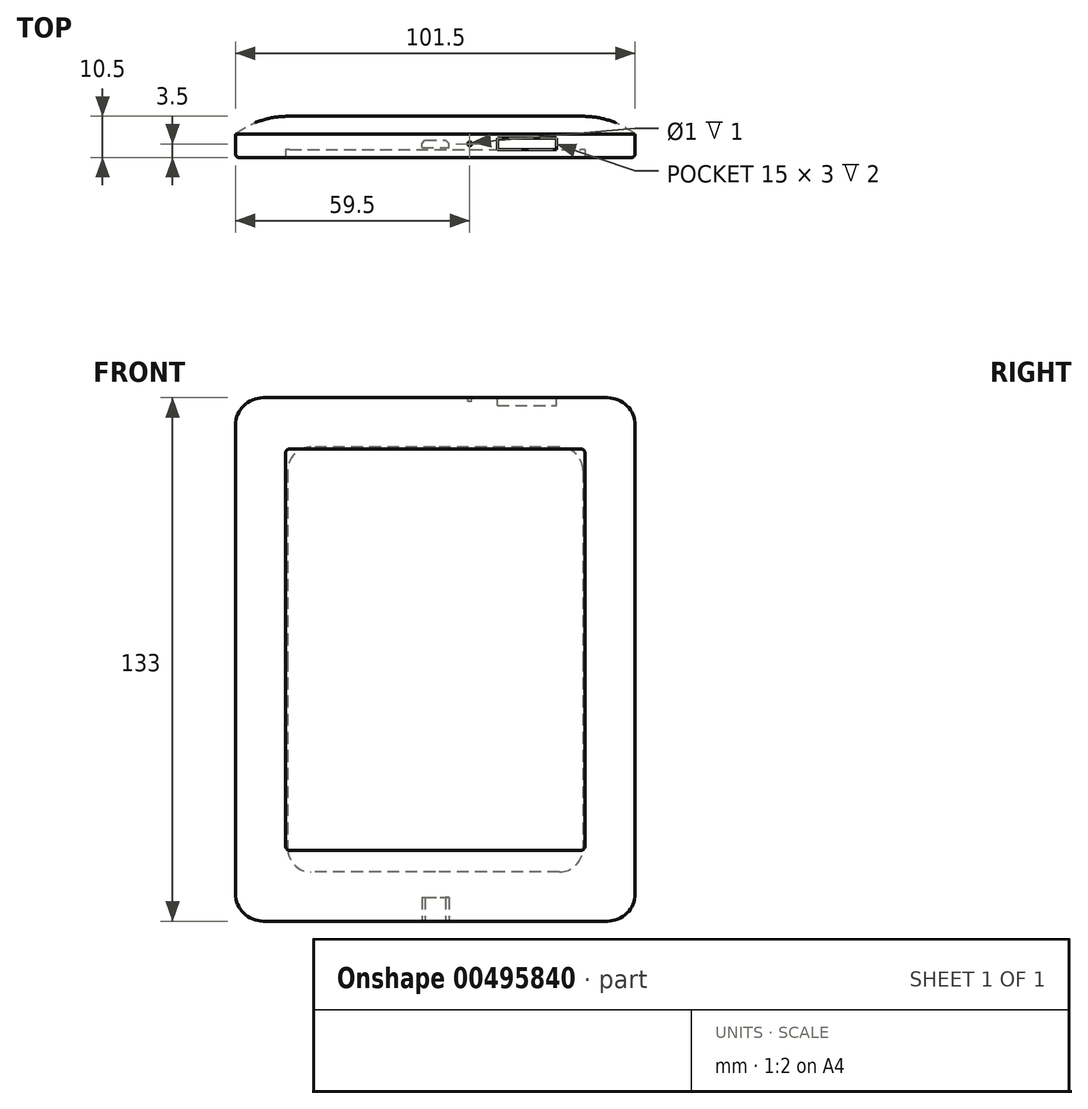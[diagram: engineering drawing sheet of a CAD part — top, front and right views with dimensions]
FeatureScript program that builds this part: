
annotation { "Feature Type Name" : "Feature", "Feature Type Description" : "" }
export const myFeature = defineFeature(function(context is Context, id is Id, definition is map)
    precondition{}
    {
        {
            var Q0;
            Q0=qCreatedBy(makeId("Front.planeOp"),FACE);
            var sketch = newSketch(context, id + "F0", { "sketchPlane" : qUnion([Q0])});
            skLineSegment(sketch, "E0.bottom", {"start": v(-43.75, 66.5) * mm, "end": v(43.75, 66.5) * mm});
            skLineSegment(sketch, "E0.top", {"start": v(-43.75, -66.5) * mm, "end": v(43.75, -66.5) * mm});
            skLineSegment(sketch, "E0.left", {"start": v(-50.75, 59.5) * mm, "end": v(-50.75, -59.5) * mm});
            skLineSegment(sketch, "E0.right", {"start": v(50.75, 59.5) * mm, "end": v(50.75, -59.5) * mm});
            skPoint(sketch, "E1.visualSharp", {"position": v(-50.75, 66.5) * mm});
            skArc(sketch, "E1.filletArc", {"start": v(-43.75, 66.5) * mm, "mid": v(-48.7, 64.45) * mm, "end": v(-50.75, 59.5) * mm});
            skPoint(sketch, "E2.visualSharp", {"position": v(50.75, 66.5) * mm});
            skArc(sketch, "E2.filletArc", {"start": v(50.75, 59.5) * mm, "mid": v(48.7, 64.45) * mm, "end": v(43.75, 66.5) * mm});
            skPoint(sketch, "E3.visualSharp", {"position": v(53.07, -60.42) * mm});
            skArc(sketch, "E3.filletArc", {"start": v(43.75, -66.5) * mm, "mid": v(48.7, -64.45) * mm, "end": v(50.75, -59.5) * mm});
            skPoint(sketch, "E4.visualSharp", {"position": v(-50.75, -66.5) * mm});
            skArc(sketch, "E4.filletArc", {"start": v(-50.75, -59.5) * mm, "mid": v(-48.7, -64.45) * mm, "end": v(-43.75, -66.5) * mm});
            skLineSegment(sketch, "E5", {"start": v(50.75, 66.5) * mm, "end": v(-50.75, -66.5) * mm, "construction": true});
            skSolve(sketch);
        }
        {
            var Q0;
            Q0 = qSketchRegion(id + "F0", true);
            extrude(context, id + "F1", {"entities" : qUnion([Q0]), "depth" : 10.5 * mm});
        }
        {
            var Q0;
            Q0=makeQuery(id+"F1.opExtrude","CAP_FACE",FACE,{"disambiguationData":[OSD([sQuery(id+"F0.wireOp",EDGE,"E0.bottom"),sQuery(id+"F0.wireOp",EDGE,"E0.top"),sQuery(id+"F0.wireOp",EDGE,"E0.left"),sQuery(id+"F0.wireOp",EDGE,"E0.right"),sQuery(id+"F0.wireOp",EDGE,"E1.filletArc"),sQuery(id+"F0.wireOp",EDGE,"E2.filletArc"),sQuery(id+"F0.wireOp",EDGE,"E3.filletArc"),sQuery(id+"F0.wireOp",EDGE,"E4.filletArc")])],"isStart":false});
            var sketch = newSketch(context, id + "F2", { "sketchPlane" : qUnion([Q0])});
            skLineSegment(sketch, "E6.bottom", {"start": v(-37, 53.5) * mm, "end": v(37, 53.5) * mm});
            skLineSegment(sketch, "E6.top", {"start": v(-37, -48.5) * mm, "end": v(37, -48.5) * mm});
            skLineSegment(sketch, "E6.left", {"start": v(-38, 52.5) * mm, "end": v(-38, -47.5) * mm});
            skLineSegment(sketch, "E6.right", {"start": v(38, 52.5) * mm, "end": v(38, -47.5) * mm});
            skLineSegment(sketch, "E7", {"start": v(0, 205.93) * mm, "end": v(0, -99.52) * mm, "construction": true});
            skLineSegment(sketch, "E8", {"start": v(-176.83, 0) * mm, "end": v(104.16, 0) * mm, "construction": true});
            skPoint(sketch, "E9.visualSharp", {"position": v(-38, 53.5) * mm});
            skArc(sketch, "E9.filletArc", {"start": v(-37, 53.5) * mm, "mid": v(-37.7, 53.2) * mm, "end": v(-38, 52.5) * mm});
            skPoint(sketch, "E10.visualSharp", {"position": v(38, 53.5) * mm});
            skArc(sketch, "E10.filletArc", {"start": v(38, 52.5) * mm, "mid": v(37.7, 53.2) * mm, "end": v(37, 53.5) * mm});
            skPoint(sketch, "E11.visualSharp", {"position": v(38, -48.5) * mm});
            skArc(sketch, "E11.filletArc", {"start": v(37, -48.5) * mm, "mid": v(37.7, -48.2) * mm, "end": v(38, -47.5) * mm});
            skPoint(sketch, "E12.visualSharp", {"position": v(-38, -48.5) * mm});
            skArc(sketch, "E12.filletArc", {"start": v(-38, -47.5) * mm, "mid": v(-37.7, -48.2) * mm, "end": v(-37, -48.5) * mm});
            skSolve(sketch);
        }
        {
            var Q0;
            Q0 = qSketchRegion(id + "F2", true);
            extrude(context, id + "F3", {"entities" : qUnion([Q0]), "operationType" : NewBodyOperationType.REMOVE, "oppositeDirection" : true, "depth" : 2 * mm});
        }
        {
            var Q0;
            Q0=makeQuery(id+"F1.opExtrude","CAP_EDGE",EDGE,{"disambiguationData":[OSD([sQuery(id+"F0.wireOp",EDGE,"E0.bottom")])],"isStart":false});
            fillet(context, id + "F4", {"entities" : qUnion([Q0]), "radius" : 1 * mm, "tangentPropagation" : true, "allowEdgeOverflow" : false});
        }
        {
            var Q0;
            Q0=qCreatedBy(makeId("Top.planeOp"),FACE);
            var sketch = newSketch(context, id + "F5", { "sketchPlane" : qUnion([Q0])});
            skArc(sketch, "E13", {"start": v(50.75, -4.5) * mm, "mid": v(44.5, -1.16) * mm, "end": v(37.5, 0) * mm});
            skLineSegment(sketch, "E14", {"start": v(37.5, 0) * mm, "end": v(50.75, 0) * mm});
            skLineSegment(sketch, "E15", {"start": v(50.75, 0) * mm, "end": v(50.75, -4.5) * mm});
            skLineSegment(sketch, "E16", {"start": v(-50.75, 0) * mm, "end": v(-37.5, 0) * mm, "construction": true});
            skSolve(sketch);
        }
        {
            var Q0;
            Q0=makeQuery(id+"F1.opExtrude","CAP_FACE",FACE,{"disambiguationData":[OSD([sQuery(id+"F0.wireOp",EDGE,"E0.bottom"),sQuery(id+"F0.wireOp",EDGE,"E0.top"),sQuery(id+"F0.wireOp",EDGE,"E0.left"),sQuery(id+"F0.wireOp",EDGE,"E0.right"),sQuery(id+"F0.wireOp",EDGE,"E1.filletArc"),sQuery(id+"F0.wireOp",EDGE,"E2.filletArc"),sQuery(id+"F0.wireOp",EDGE,"E3.filletArc"),sQuery(id+"F0.wireOp",EDGE,"E4.filletArc")])],"isStart":true});
            var sketch = newSketch(context, id + "F6", { "sketchPlane" : qUnion([Q0])});
            skLineSegment(sketch, "E17.bottom", {"start": v(-31.5, 54) * mm, "end": v(31.5, 54) * mm});
            skLineSegment(sketch, "E17.top", {"start": v(-31.5, -54) * mm, "end": v(31.5, -54) * mm});
            skLineSegment(sketch, "E17.left", {"start": v(-37.5, 48) * mm, "end": v(-37.5, -48) * mm});
            skLineSegment(sketch, "E17.right", {"start": v(37.5, 48) * mm, "end": v(37.5, -48) * mm});
            skLineSegment(sketch, "E18", {"start": v(0, 0) * mm, "end": v(154.61, 0) * mm, "construction": true});
            skPoint(sketch, "E19.visualSharp", {"position": v(-37.5, 54) * mm});
            skArc(sketch, "E19.filletArc", {"start": v(-31.5, 54) * mm, "mid": v(-35.74, 52.24) * mm, "end": v(-37.5, 48) * mm});
            skPoint(sketch, "E20.visualSharp", {"position": v(37.5, 54) * mm});
            skArc(sketch, "E20.filletArc", {"start": v(37.5, 48) * mm, "mid": v(35.74, 52.24) * mm, "end": v(31.5, 54) * mm});
            skPoint(sketch, "E21.visualSharp", {"position": v(37.5, -54) * mm});
            skArc(sketch, "E21.filletArc", {"start": v(31.5, -54) * mm, "mid": v(35.74, -52.24) * mm, "end": v(37.5, -48) * mm});
            skPoint(sketch, "E22.visualSharp", {"position": v(-37.5, -54) * mm});
            skArc(sketch, "E22.filletArc", {"start": v(-37.5, -48) * mm, "mid": v(-35.74, -52.24) * mm, "end": v(-31.5, -54) * mm});
            skSolve(sketch);
        }
        {
            var Q0;
            Q0=sQuery(id+"F5.wireOp",VERTEX,"E15.end");
            var Q1;
            Q1=qCreatedBy(makeId("Front.planeOp"),FACE);
            cPlane(context, id + "F7", {"entities" : qUnion([Q0, Q1]), "cplaneType" : CPlaneType.PLANE_POINT, "offset" : 25 * mm, "width" : 150 * mm, "height" : 150 * mm});
        }
        {
            var Q0;
            Q0=qCreatedBy(id+"F7.planeOp",FACE);
            var sketch = newSketch(context, id + "F8", { "sketchPlane" : qUnion([Q0])});
            skArc(sketch, "E23.0.0", {"start": v(-43.75, -66.5) * mm, "mid": v(-48.7, -64.45) * mm, "end": v(-50.75, -59.5) * mm});
            skLineSegment(sketch, "E23.0.1", {"start": v(-50.75, -59.5) * mm, "end": v(-50.75, 59.5) * mm});
            skArc(sketch, "E23.0.2", {"start": v(-50.75, 59.5) * mm, "mid": v(-48.7, 64.45) * mm, "end": v(-43.75, 66.5) * mm});
            skLineSegment(sketch, "E23.0.3", {"start": v(-43.75, 66.5) * mm, "end": v(43.75, 66.5) * mm});
            skArc(sketch, "E23.0.4", {"start": v(43.75, 66.5) * mm, "mid": v(48.7, 64.45) * mm, "end": v(50.75, 59.5) * mm});
            skLineSegment(sketch, "E23.0.5", {"start": v(50.75, 59.5) * mm, "end": v(50.75, -59.5) * mm});
            skArc(sketch, "E23.0.6", {"start": v(50.75, -59.5) * mm, "mid": v(48.7, -64.45) * mm, "end": v(43.75, -66.5) * mm});
            skLineSegment(sketch, "E23.0.7", {"start": v(43.75, -66.5) * mm, "end": v(-43.75, -66.5) * mm});
            skSolve(sketch);
        }
        {
            var Q0;
            Q0=makeQuery(id+"F6.imprint","IMPRINT",FACE,{"disambiguationData":[TD([[makeQuery(id+"F6.imprint","IMPRINT",EDGE,{"derivedFrom":sQuery(id+"F6.wireOp",EDGE,"E17.bottom")}),1.0]])]});
            var sketch = newSketch(context, id + "F9", { "sketchPlane" : qUnion([Q0])});
            skArc(sketch, "E24.0.0", {"start": v(43.75, -66.5) * mm, "mid": v(48.7, -64.45) * mm, "end": v(50.75, -59.5) * mm});
            skLineSegment(sketch, "E24.0.1", {"start": v(50.75, -59.5) * mm, "end": v(50.75, 59.5) * mm});
            skArc(sketch, "E24.0.2", {"start": v(50.75, 59.5) * mm, "mid": v(48.7, 64.45) * mm, "end": v(43.75, 66.5) * mm});
            skLineSegment(sketch, "E24.0.3", {"start": v(43.75, 66.5) * mm, "end": v(-43.75, 66.5) * mm});
            skArc(sketch, "E24.0.4", {"start": v(-43.75, 66.5) * mm, "mid": v(-48.7, 64.45) * mm, "end": v(-50.75, 59.5) * mm});
            skLineSegment(sketch, "E24.0.5", {"start": v(-50.75, 59.5) * mm, "end": v(-50.75, -59.5) * mm});
            skArc(sketch, "E24.0.6", {"start": v(-50.75, -59.5) * mm, "mid": v(-48.7, -64.45) * mm, "end": v(-43.75, -66.5) * mm});
            skLineSegment(sketch, "E24.0.7", {"start": v(-43.75, -66.5) * mm, "end": v(43.75, -66.5) * mm});
            skSolve(sketch);
        }
        {
            var Q1;
            Q1 = qSketchRegion(id + "F5", true);
            var Q2;
            Q2 = qConstructionFilter(qBodyType(qCreatedBy(id + "F6" ,EDGE), BodyType.WIRE), ConstructionObject.NO);
            var Q3;
            Q3 = qConstructionFilter(qBodyType(qCreatedBy(id + "F8" ,EDGE), BodyType.WIRE), ConstructionObject.NO);
            var Q4;
            Q4 = qConstructionFilter(qBodyType(qCreatedBy(id + "F9" ,EDGE), BodyType.WIRE), ConstructionObject.NO);
            loft(context, id + "F10", {"operationType" : NewBodyOperationType.REMOVE, "addGuides" : true, "sheetProfilesArray" : [{ "sheetProfileEntities" : qUnion([Q1]) }], "guidesArray" : [{ "guideEntities" : qUnion([Q2]), "guideDerivativeType" : LoftGuideDerivativeType.DEFAULT, "guideDerivativeMagnitude" : 1 }, { "guideEntities" : qUnion([Q3]), "guideDerivativeType" : LoftGuideDerivativeType.DEFAULT, "guideDerivativeMagnitude" : 1 }, { "guideEntities" : qUnion([Q4]), "guideDerivativeType" : LoftGuideDerivativeType.DEFAULT, "guideDerivativeMagnitude" : 1 }]});
        }
        {
            var Q0;
            Q0=makeQuery(id+"F1.opExtrude","SWEPT_FACE",FACE,{"disambiguationData":[OSD([sQuery(id+"F0.wireOp",EDGE,"E0.top")])]});
            var sketch = newSketch(context, id + "F11", { "sketchPlane" : qUnion([Q0])});
            skLineSegment(sketch, "E25", {"start": v(0, 7) * mm, "end": v(0, -5.98) * mm, "construction": true});
            skLineSegment(sketch, "E26.bottom", {"start": v(-3.43, 7.93) * mm, "end": v(0, 7.93) * mm});
            skLineSegment(sketch, "E26.top", {"start": v(-2.65, 6.08) * mm, "end": v(0, 6.08) * mm});
            skLineSegment(sketch, "E26.left", {"start": v(-3.43, 7.93) * mm, "end": v(-3.43, 6.9) * mm});
            skLineSegment(sketch, "E27", {"start": v(-8.15, 7) * mm, "end": v(7.58, 7) * mm, "construction": true});
            skLineSegment(sketch, "E28", {"start": v(-3.43, 6.9) * mm, "end": v(-2.65, 6.08) * mm});
            skLineSegment(sketch, "E29.MirrorCS", {"start": v(3.42, 7.93) * mm, "end": v(0, 7.93) * mm});
            skLineSegment(sketch, "E30.MirrorCS", {"start": v(3.42, 7.93) * mm, "end": v(3.42, 6.9) * mm});
            skLineSegment(sketch, "E31.MirrorCS", {"start": v(3.42, 6.9) * mm, "end": v(2.65, 6.08) * mm});
            skLineSegment(sketch, "E32.MirrorCS", {"start": v(2.65, 6.08) * mm, "end": v(0, 6.08) * mm});
            skSolve(sketch);
        }
        {
            var Q0;
            Q0 = qSketchRegion(id + "F11", true);
            extrude(context, id + "F12", {"entities" : qUnion([Q0]), "operationType" : NewBodyOperationType.REMOVE, "oppositeDirection" : true, "depth" : 6 * mm});
        }
        {
            var Q0;
            Q0=makeQuery(id+"F1.opExtrude","SWEPT_FACE",FACE,{"disambiguationData":[OSD([sQuery(id+"F0.wireOp",EDGE,"E0.bottom")])]});
            var sketch = newSketch(context, id + "F13", { "sketchPlane" : qUnion([Q0])});
            skLineSegment(sketch, "E33", {"start": v(-53.67, -7) * mm, "end": v(63.95, -7) * mm, "construction": true});
            skLineSegment(sketch, "E34.bottom", {"start": v(15.75, -5.5) * mm, "end": v(30.75, -5.5) * mm});
            skLineSegment(sketch, "E34.top", {"start": v(15.75, -8.5) * mm, "end": v(30.75, -8.5) * mm});
            skLineSegment(sketch, "E34.left", {"start": v(15.75, -5.5) * mm, "end": v(15.75, -8.5) * mm});
            skLineSegment(sketch, "E34.right", {"start": v(30.75, -5.5) * mm, "end": v(30.75, -8.5) * mm});
            skSolve(sketch);
        }
        {
            var Q0;
            Q0 = qSketchRegion(id + "F13", true);
            extrude(context, id + "F14", {"entities" : qUnion([Q0]), "operationType" : NewBodyOperationType.REMOVE, "oppositeDirection" : true, "depth" : 2 * mm});
        }
        {
            var Q0;
            Q0=makeQuery(id+"F1.opExtrude","SWEPT_FACE",FACE,{"disambiguationData":[OSD([sQuery(id+"F0.wireOp",EDGE,"E0.bottom")])]});
            var sketch = newSketch(context, id + "F15", { "sketchPlane" : qUnion([Q0])});
            skLineSegment(sketch, "E35", {"start": v(-23.84, -7) * mm, "end": v(59.8, -7) * mm, "construction": true});
            skCircle(sketch, "E36", {"center": v(8.75, -7) * mm, "radius": 0.5 * mm});
            skSolve(sketch);
        }
        {
            var Q0;
            Q0 = qSketchRegion(id + "F15", true);
            extrude(context, id + "F16", {"entities" : qUnion([Q0]), "operationType" : NewBodyOperationType.REMOVE, "oppositeDirection" : true, "depth" : 1 * mm});
        }
    });
